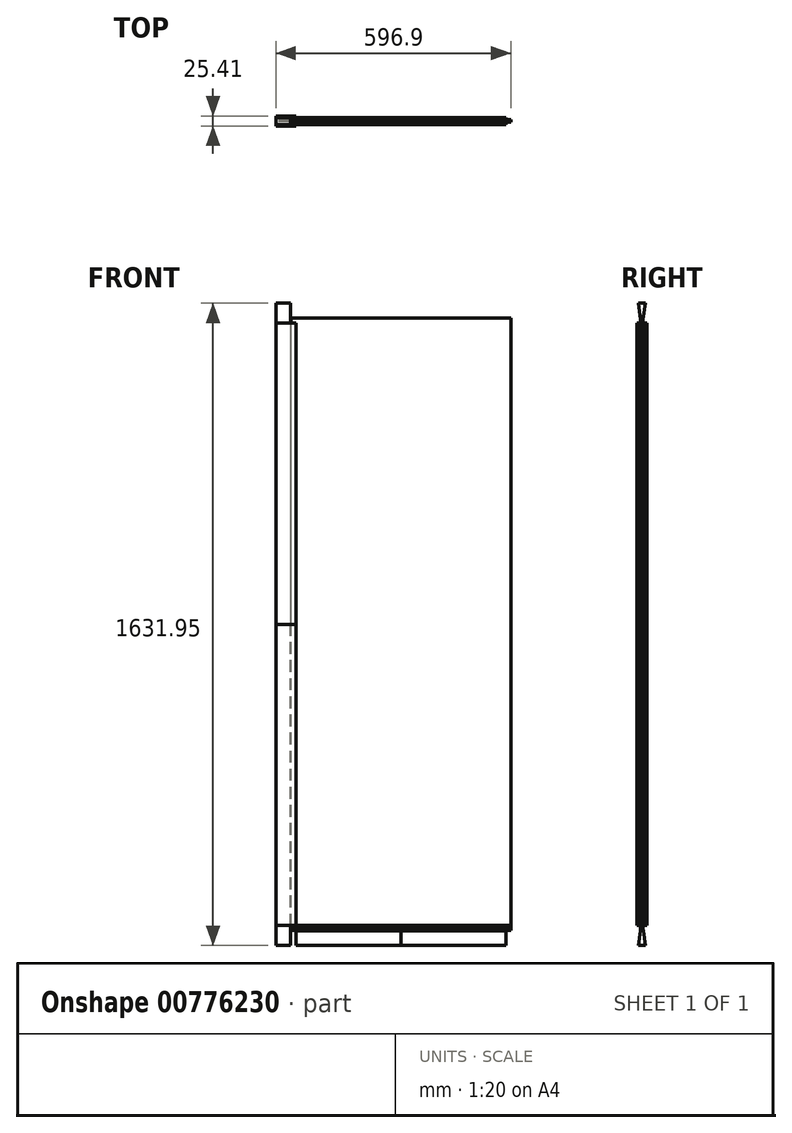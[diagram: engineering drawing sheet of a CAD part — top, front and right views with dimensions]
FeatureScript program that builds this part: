
annotation { "Feature Type Name" : "Feature", "Feature Type Description" : "" }
export const myFeature = defineFeature(function(context is Context, id is Id, definition is map)
    precondition{}
    {
        {
            var Q0;
            Q0=qCreatedBy(makeId("Front.planeOp"),FACE);
            var sketch = newSketch(context, id + "F0", { "sketchPlane" : qUnion([Q0])});
            skLineSegment(sketch, "E0.bottom", {"start": v(0, 0) * mm, "end": v(558.8, 0) * mm});
            skLineSegment(sketch, "E0.top", {"start": v(0, 1555.75) * mm, "end": v(558.8, 1555.75) * mm});
            skLineSegment(sketch, "E0.left", {"start": v(0, 0) * mm, "end": v(0, 1555.75) * mm});
            skLineSegment(sketch, "E0.right", {"start": v(558.8, 0) * mm, "end": v(558.8, 1555.75) * mm});
            skSolve(sketch);
        }
        {
            var Q0;
            Q0 = qSketchRegion(id + "F0", true);
            extrude(context, id + "F1", {"entities" : qUnion([Q0]), "oppositeDirection" : true, "depth" : 6.35 * mm, "offsetDistance" : 25.4 * mm});
        }
        {
            var Q0;
            Q0=makeQuery(id+"F1.opExtrude","CAP_EDGE",EDGE,{"disambiguationData":[OSD([sQuery(id+"F0.wireOp",EDGE,"E0.left")])],"isStart":false});
            cPoint(context, id + "F2", {"entities" : qUnion([Q0]), "parameter" : 0.5});
        }
        {
            var Q0;
            Q0=makeQuery(id+"F1.opExtrude","CAP_EDGE",EDGE,{"disambiguationData":[OSD([sQuery(id+"F0.wireOp",EDGE,"E0.left")])],"isStart":true});
            cPoint(context, id + "F3", {"entities" : qUnion([Q0]), "parameter" : 0.5});
        }
        {
            var Q0;
            Q0=makeQuery(id+"F1.opExtrude","CAP_EDGE",EDGE,{"disambiguationData":[OSD([sQuery(id+"F0.wireOp",EDGE,"E0.right")])],"isStart":true});
            cPoint(context, id + "F4", {"entities" : qUnion([Q0]), "parameter" : 0.5});
        }
        {
            var Q0;
            Q0 = qCreatedBy(id + "F2" ,VERTEX);
            var Q1;
            Q1 = qCreatedBy(id + "F3" ,VERTEX);
            var Q2;
            Q2 = qCreatedBy(id + "F4" ,VERTEX);
            cPlane(context, id + "F5", {"entities" : qUnion([Q0, Q1, Q2]), "cplaneType" : CPlaneType.THREE_POINT, "offset" : 25.4 * mm, "width" : 152.4 * mm, "height" : 152.4 * mm});
        }
        {
            var Q0;
            Q0=makeQuery(id+"F1.opExtrude","CAP_EDGE",EDGE,{"disambiguationData":[OSD([sQuery(id+"F0.wireOp",EDGE,"E0.bottom")])],"isStart":true});
            cPoint(context, id + "F6", {"entities" : qUnion([Q0]), "parameter" : 0.5});
        }
        {
            var Q0;
            Q0=makeQuery(id+"F1.opExtrude","CAP_EDGE",EDGE,{"disambiguationData":[OSD([sQuery(id+"F0.wireOp",EDGE,"E0.bottom")])],"isStart":false});
            cPoint(context, id + "F7", {"entities" : qUnion([Q0]), "parameter" : 0.5});
        }
        {
            var Q0;
            Q0=makeQuery(id+"F1.opExtrude","CAP_EDGE",EDGE,{"disambiguationData":[OSD([sQuery(id+"F0.wireOp",EDGE,"E0.top")])],"isStart":true});
            cPoint(context, id + "F8", {"entities" : qUnion([Q0]), "parameter" : 0.5});
        }
        {
            var Q0;
            Q0 = qCreatedBy(id + "F6" ,VERTEX);
            var Q1;
            Q1 = qCreatedBy(id + "F7" ,VERTEX);
            var Q2;
            Q2 = qCreatedBy(id + "F8" ,VERTEX);
            cPlane(context, id + "F9", {"entities" : qUnion([Q0, Q1, Q2]), "cplaneType" : CPlaneType.THREE_POINT, "offset" : 25.4 * mm, "width" : 152.4 * mm, "height" : 152.4 * mm});
        }
        {
            var Q0;
            Q0=qCreatedBy(id+"F9.planeOp",FACE);
            var sketch = newSketch(context, id + "F10", { "sketchPlane" : qUnion([Q0])});
            skLineSegment(sketch, "E1.bottom", {"start": v(-15.88, 12.7) * mm, "end": v(9.53, 12.7) * mm});
            skLineSegment(sketch, "E1.top", {"start": v(-15.88, -38.1) * mm, "end": v(9.53, -38.1) * mm});
            skLineSegment(sketch, "E1.left", {"start": v(-15.88, 12.7) * mm, "end": v(-15.88, -38.1) * mm});
            skLineSegment(sketch, "E1.right", {"start": v(9.53, 12.7) * mm, "end": v(9.53, -38.1) * mm});
            skLineSegment(sketch, "E2", {"start": v(-3.18, 7.87) * mm, "end": v(-3.18, 0) * mm, "construction": true});
            skSolve(sketch);
        }
        {
            var Q0;
            Q0 = qSketchRegion(id + "F10", true);
            var Q1;
            Q1=makeQuery(id+"F1.opExtrude","SWEPT_FACE",FACE,{"disambiguationData":[OSD([sQuery(id+"F0.wireOp",EDGE,"E0.left")])]});
            extrude(context, id + "F11", {"entities" : qUnion([Q0]), "endBound" : BoundingType.UP_TO_SURFACE, "depth" : 660.4 * mm, "endBoundEntityFace" : qUnion([Q1]), "hasOffset" : true, "offsetDistance" : 38.1 * mm, "offsetOppositeDirection" : true});
        }
        {
            var Q0;
            Q0=qCreatedBy(id+"F5.planeOp",FACE);
            var sketch = newSketch(context, id + "F12", { "sketchPlane" : qUnion([Q0])});
            skLineSegment(sketch, "E3.bottom", {"start": v(-38.1, -15.88) * mm, "end": v(12.7, -15.88) * mm});
            skLineSegment(sketch, "E3.top", {"start": v(-38.1, 9.53) * mm, "end": v(12.7, 9.53) * mm});
            skLineSegment(sketch, "E3.left", {"start": v(-38.1, -15.88) * mm, "end": v(-38.1, 9.53) * mm});
            skLineSegment(sketch, "E3.right", {"start": v(12.7, -15.88) * mm, "end": v(12.7, 9.53) * mm});
            skSolve(sketch);
        }
        {
            var Q0;
            Q0 = qSketchRegion(id + "F12", true);
            var Q1;
            Q1=makeQuery(id+"F11.opExtrude","SWEPT_FACE",FACE,{"disambiguationData":[OSD([sQuery(id+"F10.wireOp",EDGE,"E1.top")])]});
            var Q2;
            Q2=makeQuery(id+"F11.opExtrude","SWEPT_BODY",BODY,{"disambiguationData":[OSD([sQuery(id+"F10.wireOp",EDGE,"E1.bottom"),sQuery(id+"F10.wireOp",EDGE,"E1.top"),sQuery(id+"F10.wireOp",EDGE,"E1.left"),sQuery(id+"F10.wireOp",EDGE,"E1.right")])]});
            extrude(context, id + "F13", {"entities" : qUnion([Q0]), "depth" : 815.97 * mm, "endBoundEntityFace" : qUnion([Q1]), "endBoundEntityBody" : qUnion([Q2]), "offsetDistance" : 25.4 * mm});
        }
        {
            var Q0;
            Q0=makeQuery(id+"F1.opExtrude","SWEPT_BODY",BODY,{"disambiguationData":[OSD([sQuery(id+"F0.wireOp",EDGE,"E0.bottom"),sQuery(id+"F0.wireOp",EDGE,"E0.top"),sQuery(id+"F0.wireOp",EDGE,"E0.left"),sQuery(id+"F0.wireOp",EDGE,"E0.right")])]});
            var Q1;
            Q1=makeQuery(id+"F11.opExtrude","SWEPT_BODY",BODY,{"disambiguationData":[OSD([sQuery(id+"F10.wireOp",EDGE,"E1.bottom"),sQuery(id+"F10.wireOp",EDGE,"E1.top"),sQuery(id+"F10.wireOp",EDGE,"E1.left"),sQuery(id+"F10.wireOp",EDGE,"E1.right")])]});
            var Q2;
            Q2=makeQuery(id+"F13.opExtrude","SWEPT_BODY",BODY,{"disambiguationData":[OSD([sQuery(id+"F12.wireOp",EDGE,"E3.bottom"),sQuery(id+"F12.wireOp",EDGE,"E3.top"),sQuery(id+"F12.wireOp",EDGE,"E3.left"),sQuery(id+"F12.wireOp",EDGE,"E3.right")])]});
            booleanBodies(context, id + "F14", {"operationType" : BooleanOperationType.SUBTRACTION, "tools" : qUnion([Q0]), "targets" : qUnion([Q1, Q2]), "offset" : true, "offsetAll" : true, "offsetDistance" : 1.27 * mm, "keepTools" : true});
        }
        {
            var Q0;
            Q0=makeQuery(id+"F13.opExtrude","SWEPT_FACE",FACE,{"disambiguationData":[OSD([sQuery(id+"F12.wireOp",EDGE,"E3.left")])]});
            var sketch = newSketch(context, id + "F15", { "sketchPlane" : qUnion([Q0])});
            skPoint(sketch, "E4.0", {"position": v(-3.17, 12.7) * mm});
            skLineSegment(sketch, "E5", {"start": v(-3.17, 12.7) * mm, "end": v(-3.17, -38.1) * mm, "construction": true});
            skLineSegment(sketch, "E6.0", {"start": v(9.53, 12.7) * mm, "end": v(-15.88, 12.7) * mm, "construction": true});
            skPoint(sketch, "E7", {"position": v(-5.08, 12.7) * mm});
            skLineSegment(sketch, "E8", {"start": v(-5.08, 12.7) * mm, "end": v(-12.22, -38.1) * mm});
            skLineSegment(sketch, "E9", {"start": v(-5.08, 12.7) * mm, "end": v(-15.88, 12.7) * mm});
            skLineSegment(sketch, "E10.MirrorCS", {"start": v(-15.87, 12.7) * mm, "end": v(9.53, 12.7) * mm, "construction": true});
            skLineSegment(sketch, "E11.MirrorCS", {"start": v(-1.27, 12.7) * mm, "end": v(5.87, -38.1) * mm});
            skLineSegment(sketch, "E12.MirrorCS", {"start": v(-1.27, 12.7) * mm, "end": v(9.53, 12.7) * mm});
            skSolve(sketch);
        }
        {
            var Q0;
            {var subQ0=sQuery(id+"F15.wireOp",EDGE,"E8");Q0=makeQuery(id+"F15.imprint","IMPRINT",FACE,{"disambiguationData":[TD([[makeQuery(id+"F15.imprint","IMPRINT",EDGE,{"derivedFrom":subQ0}),-1.0]])]});}
            var Q1;
            {var subQ0=sQuery(id+"F15.wireOp",EDGE,"E11.MirrorCS");Q1=makeQuery(id+"F15.imprint","IMPRINT",FACE,{"disambiguationData":[TD([[makeQuery(id+"F15.imprint","IMPRINT",EDGE,{"derivedFrom":subQ0}),1.0]])]});}
            extrude(context, id + "F16", {"entities" : qUnion([Q0, Q1]), "operationType" : NewBodyOperationType.REMOVE, "endBound" : BoundingType.THROUGH_ALL, "oppositeDirection" : true, "depth" : 25.4 * mm, "offsetDistance" : 25.4 * mm});
        }
        {
            var Q0;
            {var subQ0=sQuery(id+"F12.wireOp",EDGE,"E3.right");var subQ1=makeQuery(id+"F13.opExtrude","SWEPT_FACE",FACE,{"disambiguationData":[OSD([subQ0])]});Q0=makeQuery(id+"F16.boolean.opBoolean","SPLIT",FACE,{"disambiguationData":[TD([makeQuery(id+"F16.opExtrude","SWEPT_FACE",FACE,{"disambiguationData":[OSD([sQuery(id+"F15.wireOp",EDGE,"E8")])]})])],"derivedFrom":subQ1});}
            var Q1;
            {var subQ2=sQuery(id+"F0.wireOp",EDGE,"E0.left");var subQ4=makeQuery(id+"F14.tempBoolean.opBoolean","COPY",FACE,{"disambiguationData":[TD([makeQuery(id+"F13.opExtrude","CAP_FACE",FACE,{"disambiguationData":[OSD([sQuery(id+"F12.wireOp",EDGE,"E3.bottom"),sQuery(id+"F12.wireOp",EDGE,"E3.top"),sQuery(id+"F12.wireOp",EDGE,"E3.left"),sQuery(id+"F12.wireOp",EDGE,"E3.right")])],"isStart":true})])],"derivedFrom":makeQuery(id+"F14.offsetTempBody.opPattern","COPY",FACE,{"derivedFrom":makeQuery(id+"F1.opExtrude","SWEPT_FACE",FACE,{"disambiguationData":[OSD([subQ2])]}),"instanceName":"1"})});Q1=makeQuery(id+"F19.boolean.opBoolean","MERGE",FACE,{"derivedFrom":[subQ4,makeQuery(id+"F19.opPattern","COPY",FACE,{"derivedFrom":subQ4,"instanceName":"1"})]});}
            extrude(context, id + "F17", {"entities" : qUnion([Q0]), "operationType" : NewBodyOperationType.REMOVE, "endBound" : BoundingType.UP_TO_SURFACE, "oppositeDirection" : true, "depth" : 25.4 * mm, "endBoundEntityFace" : qUnion([Q1]), "offsetDistance" : 25.4 * mm});
        }
        {
            var Q0;
            Q0=makeQuery(id+"F13.opExtrude","SWEPT_BODY",BODY,{"disambiguationData":[OSD([sQuery(id+"F12.wireOp",EDGE,"E3.bottom"),sQuery(id+"F12.wireOp",EDGE,"E3.top"),sQuery(id+"F12.wireOp",EDGE,"E3.left"),sQuery(id+"F12.wireOp",EDGE,"E3.right")])]});
            var Q1;
            Q1=makeQuery(id+"F11.opExtrude","SWEPT_BODY",BODY,{"disambiguationData":[OSD([sQuery(id+"F10.wireOp",EDGE,"E1.bottom"),sQuery(id+"F10.wireOp",EDGE,"E1.top"),sQuery(id+"F10.wireOp",EDGE,"E1.left"),sQuery(id+"F10.wireOp",EDGE,"E1.right")])]});
            booleanBodies(context, id + "F18", {"operationType" : BooleanOperationType.SUBTRACTION, "tools" : qUnion([Q0]), "targets" : qUnion([Q1]), "keepTools" : true});
        }
        {
            var Q0;
            Q0=makeQuery(id+"F13.opExtrude","SWEPT_BODY",BODY,{"disambiguationData":[OSD([sQuery(id+"F12.wireOp",EDGE,"E3.bottom"),sQuery(id+"F12.wireOp",EDGE,"E3.top"),sQuery(id+"F12.wireOp",EDGE,"E3.left"),sQuery(id+"F12.wireOp",EDGE,"E3.right")])]});
            var Q1;
            Q1=qCreatedBy(id+"F5.planeOp",FACE);
            mirror(context, id + "F19", {"operationType" : NewBodyOperationType.ADD, "entities" : qUnion([Q0]), "mirrorPlane" : qUnion([Q1])});
        }
        {
            var Q0;
            Q0=makeQuery(id+"F11.opExtrude","SWEPT_BODY",BODY,{"disambiguationData":[OSD([sQuery(id+"F10.wireOp",EDGE,"E1.bottom"),sQuery(id+"F10.wireOp",EDGE,"E1.top"),sQuery(id+"F10.wireOp",EDGE,"E1.left"),sQuery(id+"F10.wireOp",EDGE,"E1.right")])]});
            var Q1;
            Q1=qCreatedBy(id+"F9.planeOp",FACE);
            mirror(context, id + "F20", {"operationType" : NewBodyOperationType.ADD, "entities" : qUnion([Q0]), "mirrorPlane" : qUnion([Q1])});
        }
    });
